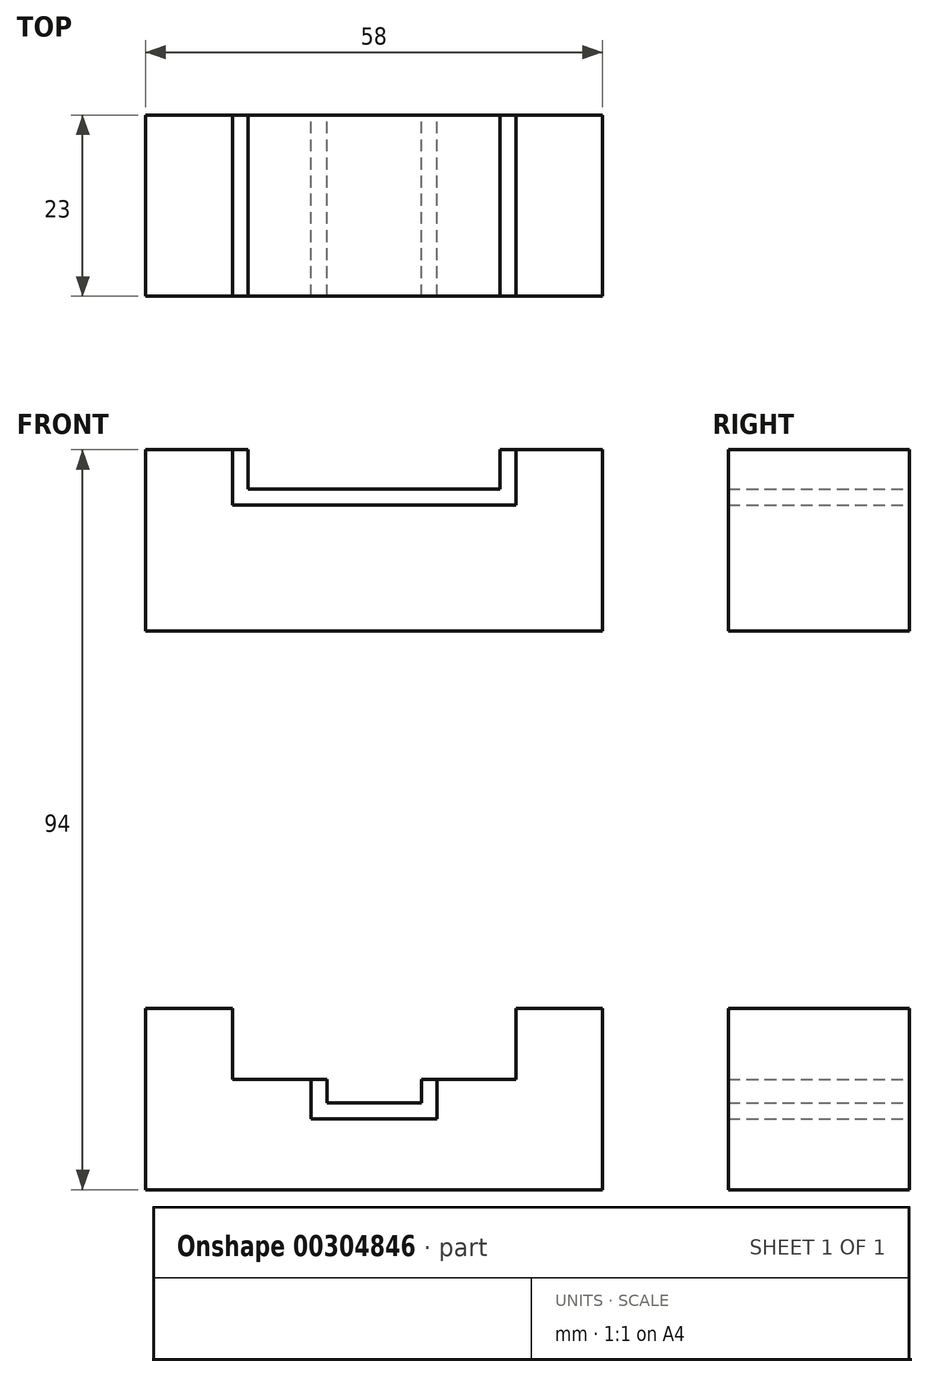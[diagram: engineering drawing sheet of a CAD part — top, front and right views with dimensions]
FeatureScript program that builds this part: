
annotation { "Feature Type Name" : "Feature", "Feature Type Description" : "" }
export const myFeature = defineFeature(function(context is Context, id is Id, definition is map)
    precondition{}
    {
        {
            var Q0;
            Q0=qCreatedBy(makeId("Front.planeOp"),FACE);
            var sketch = newSketch(context, id + "F0", { "sketchPlane" : qUnion([Q0])});
            skLineSegment(sketch, "E0.bottom", {"start": v(0, 0) * mm, "end": v(200, 0) * mm, "construction": true});
            skLineSegment(sketch, "E0.top", {"start": v(0, 300) * mm, "end": v(200, 300) * mm, "construction": true});
            skLineSegment(sketch, "E0.left", {"start": v(0, 0) * mm, "end": v(0, 300) * mm, "construction": true});
            skLineSegment(sketch, "E0.right", {"start": v(200, 0) * mm, "end": v(200, 300) * mm, "construction": true});
            skLineSegment(sketch, "E1.bottom", {"start": v(30, 270) * mm, "end": v(88, 270) * mm});
            skLineSegment(sketch, "E1.top", {"start": v(30, 247) * mm, "end": v(88, 247) * mm});
            skLineSegment(sketch, "E1.left", {"start": v(30, 270) * mm, "end": v(30, 247) * mm});
            skLineSegment(sketch, "E1.right", {"start": v(88, 270) * mm, "end": v(88, 247) * mm});
            skLineSegment(sketch, "E2.0.1.0", {"start": v(30, 176) * mm, "end": v(88, 176) * mm});
            skLineSegment(sketch, "E2.0.1.1", {"start": v(88, 199) * mm, "end": v(88, 176) * mm});
            skLineSegment(sketch, "E2.0.1.2", {"start": v(30, 199) * mm, "end": v(88, 199) * mm});
            skLineSegment(sketch, "E2.0.1.3", {"start": v(30, 199) * mm, "end": v(30, 176) * mm});
            skLineSegment(sketch, "E2.0.2.0", {"start": v(30, 105) * mm, "end": v(88, 105) * mm});
            skLineSegment(sketch, "E2.0.2.1", {"start": v(88, 128) * mm, "end": v(88, 105) * mm});
            skLineSegment(sketch, "E2.0.2.2", {"start": v(30, 128) * mm, "end": v(88, 128) * mm});
            skLineSegment(sketch, "E2.0.2.3", {"start": v(30, 128) * mm, "end": v(30, 105) * mm});
            skLineSegment(sketch, "E2.0.3.0", {"start": v(30, 34) * mm, "end": v(88, 34) * mm});
            skLineSegment(sketch, "E2.0.3.1", {"start": v(88, 57) * mm, "end": v(88, 34) * mm});
            skLineSegment(sketch, "E2.0.3.2", {"start": v(30, 57) * mm, "end": v(88, 57) * mm});
            skLineSegment(sketch, "E2.0.3.3", {"start": v(30, 57) * mm, "end": v(30, 34) * mm});
            skLineSegment(sketch, "E2.direction1", {"start": v(30, 247) * mm, "end": v(55, 247) * mm, "construction": true});
            skLineSegment(sketch, "E2.direction2", {"start": v(30, 247) * mm, "end": v(30, 176) * mm, "construction": true});
            skSolve(sketch);
        }
        {
            var Q0;
            Q0=qCreatedBy(makeId("Front.planeOp"),FACE);
            var sketch = newSketch(context, id + "F1", { "sketchPlane" : qUnion([Q0])});
            skLineSegment(sketch, "E3.bottom", {"start": v(41, 270) * mm, "end": v(77, 270) * mm});
            skLineSegment(sketch, "E3.top", {"start": v(41, 263) * mm, "end": v(77, 263) * mm});
            skLineSegment(sketch, "E3.left", {"start": v(41, 270) * mm, "end": v(41, 263) * mm});
            skLineSegment(sketch, "E3.right", {"start": v(77, 270) * mm, "end": v(77, 263) * mm});
            skPoint(sketch, "E4", {"position": v(59, 270) * mm});
            skPoint(sketch, "E5", {"position": v(59, 199) * mm});
            skPoint(sketch, "E6", {"position": v(59, 128) * mm});
            skPoint(sketch, "E7", {"position": v(59, 57) * mm});
            skLineSegment(sketch, "E8.0", {"start": v(75, 270) * mm, "end": v(75, 265) * mm});
            skLineSegment(sketch, "E8.1", {"start": v(43, 265) * mm, "end": v(75, 265) * mm});
            skLineSegment(sketch, "E8.2", {"start": v(43, 270) * mm, "end": v(43, 265) * mm});
            skLineSegment(sketch, "E9.bottom", {"start": v(30, 270) * mm, "end": v(88, 270) * mm});
            skLineSegment(sketch, "E9.top", {"start": v(30, 247) * mm, "end": v(88, 247) * mm});
            skLineSegment(sketch, "E9.left", {"start": v(30, 270) * mm, "end": v(30, 247) * mm});
            skLineSegment(sketch, "E9.right", {"start": v(88, 270) * mm, "end": v(88, 247) * mm});
            skLineSegment(sketch, "E10.bottom", {"start": v(41, 199) * mm, "end": v(77, 199) * mm});
            skLineSegment(sketch, "E10.top", {"start": v(41, 190) * mm, "end": v(77, 190) * mm});
            skLineSegment(sketch, "E10.left", {"start": v(41, 199) * mm, "end": v(41, 190) * mm});
            skLineSegment(sketch, "E10.right", {"start": v(77, 199) * mm, "end": v(77, 190) * mm});
            skLineSegment(sketch, "E11.bottom", {"start": v(53, 187) * mm, "end": v(65, 187) * mm});
            skLineSegment(sketch, "E11.top", {"start": v(53, 190) * mm, "end": v(65, 190) * mm});
            skLineSegment(sketch, "E11.left", {"start": v(65, 190) * mm, "end": v(65, 187) * mm});
            skLineSegment(sketch, "E11.right", {"start": v(53, 190) * mm, "end": v(53, 187) * mm});
            skPoint(sketch, "E12", {"position": v(59, 187) * mm});
            skPoint(sketch, "E13", {"position": v(59, 190) * mm});
            skLineSegment(sketch, "E14.bottom", {"start": v(88, 199) * mm, "end": v(30, 199) * mm});
            skLineSegment(sketch, "E14.top", {"start": v(88, 176) * mm, "end": v(30, 176) * mm});
            skLineSegment(sketch, "E14.left", {"start": v(88, 199) * mm, "end": v(88, 176) * mm});
            skLineSegment(sketch, "E14.right", {"start": v(30, 199) * mm, "end": v(30, 176) * mm});
            skLineSegment(sketch, "E15.0", {"start": v(43, 199) * mm, "end": v(43, 192) * mm});
            skLineSegment(sketch, "E15.1", {"start": v(43, 192) * mm, "end": v(75, 192) * mm});
            skLineSegment(sketch, "E15.2", {"start": v(75, 199) * mm, "end": v(75, 192) * mm});
            skLineSegment(sketch, "E16.0", {"start": v(67, 190) * mm, "end": v(67, 185) * mm});
            skLineSegment(sketch, "E16.1", {"start": v(51, 185) * mm, "end": v(67, 185) * mm});
            skLineSegment(sketch, "E16.2", {"start": v(51, 190) * mm, "end": v(51, 185) * mm});
            skSolve(sketch);
        }
        {
            var Q0;
            {var subQ5=sQuery(id+"F1.wireOp",EDGE,"E10.left");Q0=makeQuery(id+"F1.imprint","IMPRINT",FACE,{"disambiguationData":[TD([[makeQuery(id+"F1.imprint","IMPRINT",EDGE,{"derivedFrom":subQ5}),-1.0]])]});}
            var Q1;
            Q1=makeQuery(id+"F1.imprint","IMPRINT",FACE,{"disambiguationData":[TD([[makeQuery(id+"F1.imprint","IMPRINT",EDGE,{"derivedFrom":sQuery(id+"F1.wireOp",EDGE,"E3.top")}),-1.0]])]});
            extrude(context, id + "F2", {"entities" : qUnion([Q0, Q1]), "depth" : 23 * mm});
        }
        {
            var Q0;
            Q0=makeQuery(id+"F1.imprint","IMPRINT",FACE,{"disambiguationData":[TD([[makeQuery(id+"F1.imprint","IMPRINT",EDGE,{"derivedFrom":sQuery(id+"F1.wireOp",EDGE,"E3.top")}),1.0]])]});
            var Q1;
            Q1=makeQuery(id+"F1.imprint","IMPRINT",FACE,{"disambiguationData":[TD([[makeQuery(id+"F1.imprint","IMPRINT",EDGE,{"derivedFrom":sQuery(id+"F1.wireOp",EDGE,"E11.bottom")}),-1.0]])]});
            extrude(context, id + "F3", {"entities" : qUnion([Q0, Q1]), "depth" : 23 * mm});
        }
    });
